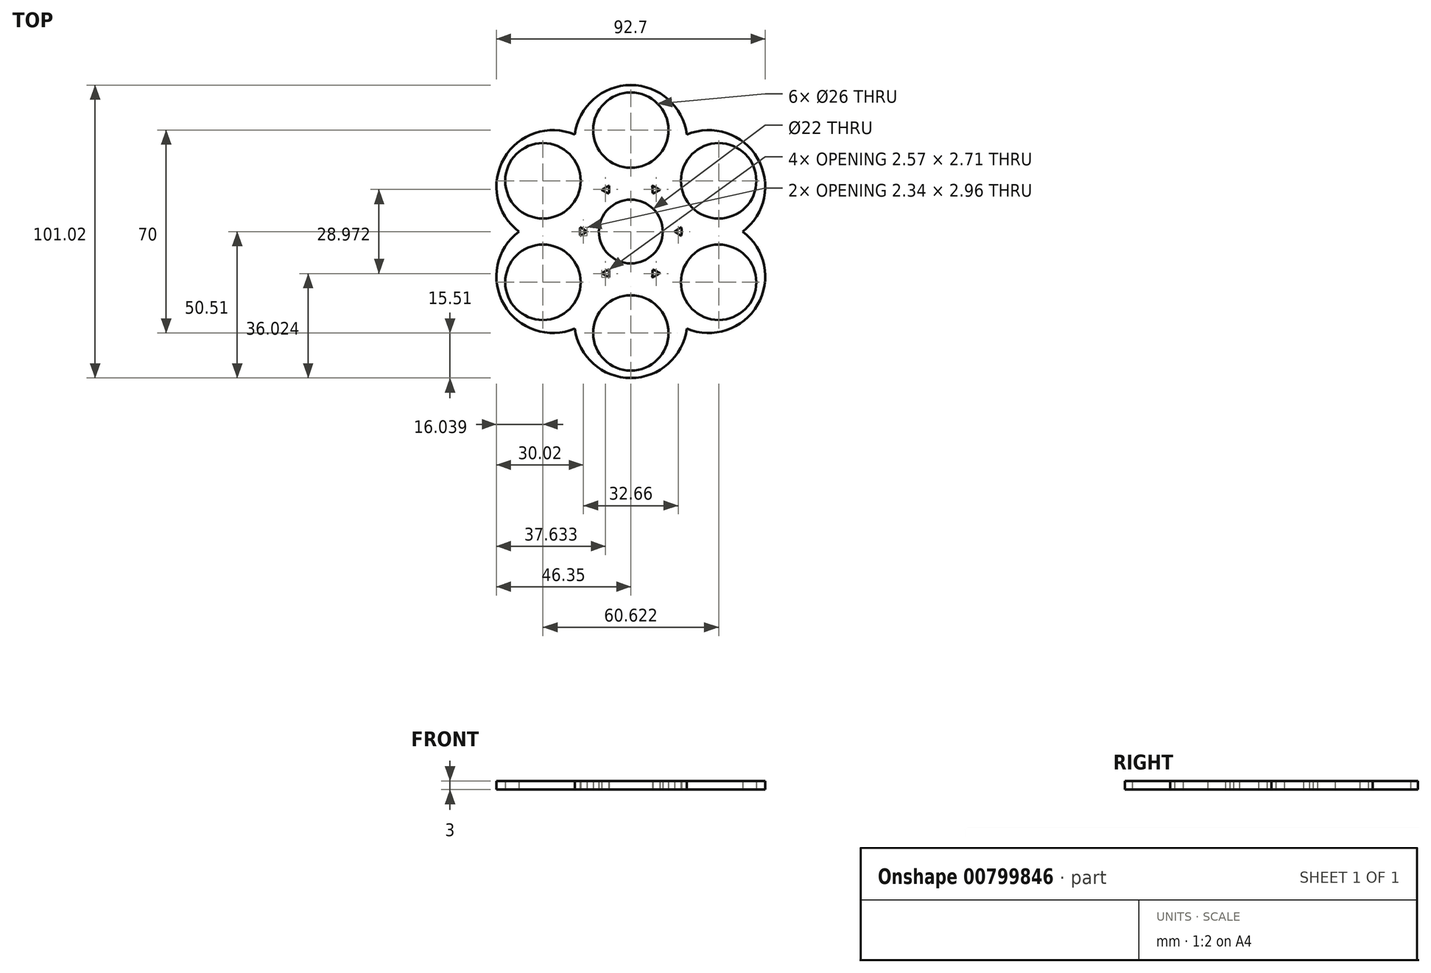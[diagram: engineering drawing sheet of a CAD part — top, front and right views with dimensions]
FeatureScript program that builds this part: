
annotation { "Feature Type Name" : "Feature", "Feature Type Description" : "" }
export const myFeature = defineFeature(function(context is Context, id is Id, definition is map)
    precondition{}
    {
        {
            var Q0;
            Q0=qCreatedBy(makeId("Top.planeOp"),FACE);
            var sketch = newSketch(context, id + "F0", { "sketchPlane" : qUnion([Q0])});
            skArc(sketch, "E0", {"start": v(5.5, 9.53) * mm, "mid": v(0, 11) * mm, "end": v(-5.5, 9.53) * mm});
            skArc(sketch, "E1", {"start": v(10, 14.36) * mm, "mid": v(9.38, 14.77) * mm, "end": v(8.75, 15.16) * mm});
            skCircle(sketch, "E2", {"center": v(0, 35) * mm, "radius": 13 * mm});
            skArc(sketch, "E3", {"start": v(7.58, 13.13) * mm, "mid": v(8.81, 13.7) * mm, "end": v(10, 14.36) * mm});
            skArc(sketch, "E4.trimOffspring", {"start": v(-8.75, 15.16) * mm, "mid": v(-9.38, 14.77) * mm, "end": v(-10, 14.36) * mm});
            skArc(sketch, "E5.trimOffspring", {"start": v(-10, 14.36) * mm, "mid": v(-8.81, 13.7) * mm, "end": v(-7.58, 13.13) * mm});
            skArc(sketch, "E6.trimOffspring", {"start": v(19.31, 33.45) * mm, "mid": v(0, 50.5) * mm, "end": v(-19.31, 33.45) * mm});
            skArc(sketch, "E7.1.0", {"start": v(-19.31, 33.45) * mm, "mid": v(-43.74, 25.25) * mm, "end": v(-38.62, 0) * mm});
            skCircle(sketch, "E7.1.1", {"center": v(-30.31, 17.5) * mm, "radius": 13 * mm});
            skArc(sketch, "E7.1.2", {"start": v(-7.58, 13.13) * mm, "mid": v(-7.46, 14.48) * mm, "end": v(-7.43, 15.84) * mm});
            skArc(sketch, "E7.1.3", {"start": v(-7.43, 15.84) * mm, "mid": v(-8.1, 15.51) * mm, "end": v(-8.75, 15.16) * mm});
            skArc(sketch, "E7.1.4", {"start": v(-5.5, 9.53) * mm, "mid": v(-9.53, 5.5) * mm, "end": v(-11, 0) * mm});
            skArc(sketch, "E7.1.5", {"start": v(-17.44, -1.48) * mm, "mid": v(-16.27, -0.78) * mm, "end": v(-15.16, 0) * mm});
            skArc(sketch, "E7.1.6", {"start": v(-17.5, 0) * mm, "mid": v(-17.48, -0.74) * mm, "end": v(-17.44, -1.48) * mm});
            skArc(sketch, "E7.2.0", {"start": v(-38.62, 0) * mm, "mid": v(-43.74, -25.25) * mm, "end": v(-19.31, -33.45) * mm});
            skCircle(sketch, "E7.2.1", {"center": v(-30.31, -17.5) * mm, "radius": 13 * mm});
            skArc(sketch, "E7.2.2", {"start": v(-15.16, 0) * mm, "mid": v(-16.27, 0.78) * mm, "end": v(-17.44, 1.48) * mm});
            skArc(sketch, "E7.2.3", {"start": v(-17.44, 1.48) * mm, "mid": v(-17.48, 0.74) * mm, "end": v(-17.5, 0) * mm});
            skArc(sketch, "E7.2.4", {"start": v(-11, 0) * mm, "mid": v(-9.53, -5.5) * mm, "end": v(-5.5, -9.53) * mm});
            skArc(sketch, "E7.2.5", {"start": v(-7.43, -15.84) * mm, "mid": v(-7.46, -14.48) * mm, "end": v(-7.58, -13.13) * mm});
            skArc(sketch, "E7.2.6", {"start": v(-8.75, -15.16) * mm, "mid": v(-8.1, -15.51) * mm, "end": v(-7.43, -15.84) * mm});
            skArc(sketch, "E7.3.0", {"start": v(-19.31, -33.45) * mm, "mid": v(0, -50.5) * mm, "end": v(19.31, -33.45) * mm});
            skCircle(sketch, "E7.3.1", {"center": v(0, -35) * mm, "radius": 13 * mm});
            skArc(sketch, "E7.3.2", {"start": v(-7.58, -13.13) * mm, "mid": v(-8.81, -13.7) * mm, "end": v(-10, -14.36) * mm});
            skArc(sketch, "E7.3.3", {"start": v(-10, -14.36) * mm, "mid": v(-9.38, -14.77) * mm, "end": v(-8.75, -15.16) * mm});
            skArc(sketch, "E7.3.4", {"start": v(-5.5, -9.53) * mm, "mid": v(0, -11) * mm, "end": v(5.5, -9.53) * mm});
            skArc(sketch, "E7.3.5", {"start": v(10, -14.36) * mm, "mid": v(8.81, -13.7) * mm, "end": v(7.58, -13.13) * mm});
            skArc(sketch, "E7.3.6", {"start": v(8.75, -15.16) * mm, "mid": v(9.38, -14.77) * mm, "end": v(10, -14.36) * mm});
            skArc(sketch, "E7.4.0", {"start": v(19.31, -33.45) * mm, "mid": v(43.74, -25.25) * mm, "end": v(38.62, 0) * mm});
            skCircle(sketch, "E7.4.1", {"center": v(30.31, -17.5) * mm, "radius": 13 * mm});
            skArc(sketch, "E7.4.2", {"start": v(7.58, -13.13) * mm, "mid": v(7.46, -14.48) * mm, "end": v(7.43, -15.84) * mm});
            skArc(sketch, "E7.4.3", {"start": v(7.43, -15.84) * mm, "mid": v(8.1, -15.51) * mm, "end": v(8.75, -15.16) * mm});
            skArc(sketch, "E7.4.4", {"start": v(5.5, -9.53) * mm, "mid": v(9.53, -5.5) * mm, "end": v(11, 0) * mm});
            skArc(sketch, "E7.4.5", {"start": v(17.44, 1.48) * mm, "mid": v(16.27, 0.78) * mm, "end": v(15.16, 0) * mm});
            skArc(sketch, "E7.4.6", {"start": v(17.5, 0) * mm, "mid": v(17.48, 0.74) * mm, "end": v(17.44, 1.48) * mm});
            skArc(sketch, "E7.5.0", {"start": v(38.62, 0) * mm, "mid": v(43.74, 25.25) * mm, "end": v(19.31, 33.45) * mm});
            skCircle(sketch, "E7.5.1", {"center": v(30.31, 17.5) * mm, "radius": 13 * mm});
            skArc(sketch, "E7.5.2", {"start": v(15.16, 0) * mm, "mid": v(16.27, -0.78) * mm, "end": v(17.44, -1.48) * mm});
            skArc(sketch, "E7.5.3", {"start": v(17.44, -1.48) * mm, "mid": v(17.48, -0.74) * mm, "end": v(17.5, 0) * mm});
            skArc(sketch, "E7.5.4", {"start": v(11, 0) * mm, "mid": v(9.53, 5.5) * mm, "end": v(5.5, 9.53) * mm});
            skArc(sketch, "E7.5.5", {"start": v(7.43, 15.84) * mm, "mid": v(7.46, 14.48) * mm, "end": v(7.58, 13.13) * mm});
            skArc(sketch, "E7.5.6", {"start": v(8.75, 15.16) * mm, "mid": v(8.1, 15.51) * mm, "end": v(7.43, 15.84) * mm});
            skSolve(sketch);
        }
        {
            var Q0;
            Q0 = qSketchRegion(id + "F0", true);
            extrude(context, id + "F1", {"entities" : qUnion([Q0]), "depth" : 3 * mm, "offsetDistance" : 25 * mm});
        }
    });
